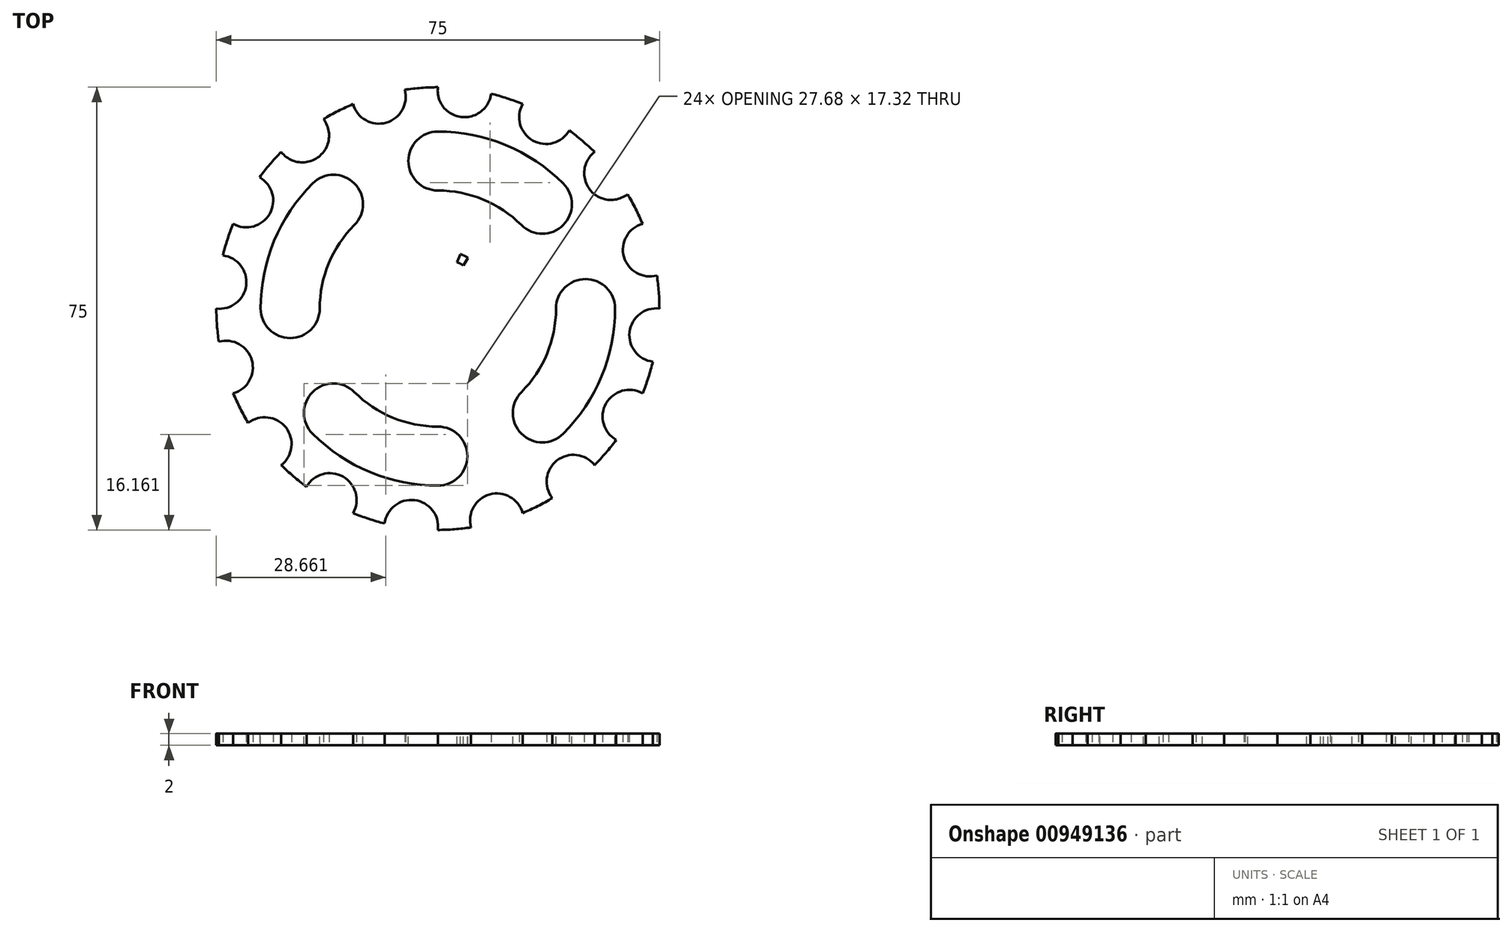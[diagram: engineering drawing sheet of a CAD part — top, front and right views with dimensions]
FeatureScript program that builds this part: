
annotation { "Feature Type Name" : "Feature", "Feature Type Description" : "" }
export const myFeature = defineFeature(function(context is Context, id is Id, definition is map)
    precondition{}
    {
        {
            var Q0;
            Q0=qCreatedBy(makeId("Top.planeOp"),FACE);
            var sketch = newSketch(context, id + "F0", { "sketchPlane" : qUnion([Q0])});
            skCircle(sketch, "E0", {"center": v(0, 0) * mm, "radius": 37.5 * mm});
            skArc(sketch, "E1", {"start": v(0, 37.5) * mm, "mid": v(3.95, 32.45) * mm, "end": v(9, 36.4) * mm});
            skArc(sketch, "E2.1.0", {"start": v(-14.35, 34.65) * mm, "mid": v(-8.77, 31.5) * mm, "end": v(-5.62, 37.08) * mm});
            skArc(sketch, "E2.2.0", {"start": v(-26.52, 26.52) * mm, "mid": v(-20.15, 25.74) * mm, "end": v(-19.38, 32.1) * mm});
            skArc(sketch, "E2.3.0", {"start": v(-34.65, 14.35) * mm, "mid": v(-28.47, 16.07) * mm, "end": v(-30.19, 22.25) * mm});
            skArc(sketch, "E2.4.0", {"start": v(-37.5, 0) * mm, "mid": v(-32.45, 3.95) * mm, "end": v(-36.4, 9) * mm});
            skArc(sketch, "E2.5.0", {"start": v(-34.65, -14.35) * mm, "mid": v(-31.5, -8.77) * mm, "end": v(-37.08, -5.62) * mm});
            skArc(sketch, "E2.6.0", {"start": v(-26.52, -26.52) * mm, "mid": v(-25.74, -20.15) * mm, "end": v(-32.1, -19.38) * mm});
            skArc(sketch, "E2.7.0", {"start": v(-14.35, -34.65) * mm, "mid": v(-16.07, -28.47) * mm, "end": v(-22.25, -30.19) * mm});
            skArc(sketch, "E2.8.0", {"start": v(0, -37.5) * mm, "mid": v(-3.95, -32.45) * mm, "end": v(-9, -36.4) * mm});
            skArc(sketch, "E2.9.0", {"start": v(14.35, -34.65) * mm, "mid": v(8.77, -31.5) * mm, "end": v(5.62, -37.08) * mm});
            skArc(sketch, "E2.10.0", {"start": v(26.52, -26.52) * mm, "mid": v(20.15, -25.74) * mm, "end": v(19.38, -32.1) * mm});
            skArc(sketch, "E2.11.0", {"start": v(34.65, -14.35) * mm, "mid": v(28.47, -16.07) * mm, "end": v(30.19, -22.25) * mm});
            skArc(sketch, "E2.12.0", {"start": v(37.5, 0) * mm, "mid": v(32.45, -3.95) * mm, "end": v(36.4, -9) * mm});
            skArc(sketch, "E2.13.0", {"start": v(34.65, 14.35) * mm, "mid": v(31.5, 8.77) * mm, "end": v(37.08, 5.62) * mm});
            skArc(sketch, "E2.14.0", {"start": v(26.52, 26.52) * mm, "mid": v(25.74, 20.15) * mm, "end": v(32.1, 19.38) * mm});
            skArc(sketch, "E2.15.0", {"start": v(14.35, 34.65) * mm, "mid": v(16.07, 28.47) * mm, "end": v(22.25, 30.19) * mm});
            skSolve(sketch);
        }
        {
            var Q0;
            {var subQ2=sQuery(id+"F0.wireOp",EDGE,"E1");Q0=makeQuery(id+"F0.imprint","IMPRINT",FACE,{"disambiguationData":[TD([[makeQuery(id+"F0.imprint","IMPRINT",EDGE,{"derivedFrom":subQ2}),-1.0]])]});}
            extrude(context, id + "F1", {"entities" : qUnion([Q0]), "depth" : 2 * mm, "offsetDistance" : 25 * mm});
        }
        {
            var Q0;
            Q0=makeQuery(id+"F1.opExtrude","CAP_FACE",FACE,{"disambiguationData":[OSD([sQuery(id+"F0.wireOp",EDGE,"E0"),sQuery(id+"F0.wireOp",EDGE,"E1"),sQuery(id+"F0.wireOp",EDGE,"E2.1.0"),sQuery(id+"F0.wireOp",EDGE,"E2.2.0"),sQuery(id+"F0.wireOp",EDGE,"E2.3.0"),sQuery(id+"F0.wireOp",EDGE,"E2.4.0"),sQuery(id+"F0.wireOp",EDGE,"E2.5.0"),sQuery(id+"F0.wireOp",EDGE,"E2.6.0"),sQuery(id+"F0.wireOp",EDGE,"E2.7.0"),sQuery(id+"F0.wireOp",EDGE,"E2.8.0"),sQuery(id+"F0.wireOp",EDGE,"E2.9.0"),sQuery(id+"F0.wireOp",EDGE,"E2.10.0"),sQuery(id+"F0.wireOp",EDGE,"E2.11.0"),sQuery(id+"F0.wireOp",EDGE,"E2.12.0"),sQuery(id+"F0.wireOp",EDGE,"E2.13.0"),sQuery(id+"F0.wireOp",EDGE,"E2.14.0"),sQuery(id+"F0.wireOp",EDGE,"E2.15.0")])],"isStart":false});
            var sketch = newSketch(context, id + "F2", { "sketchPlane" : qUnion([Q0])});
            skCircle(sketch, "E3", {"center": v(0, 0) * mm, "radius": 10 * mm});
            skArc(sketch, "E4", {"start": v(14.14, 14.14) * mm, "mid": v(7.65, 18.48) * mm, "end": v(0, 20) * mm});
            skArc(sketch, "E5", {"start": v(0, 30) * mm, "mid": v(-5, 25) * mm, "end": v(0, 20) * mm});
            skArc(sketch, "E6.1.0", {"start": v(-14.14, 14.14) * mm, "mid": v(-14.14, 21.21) * mm, "end": v(-21.21, 21.21) * mm});
            skArc(sketch, "E6.2.0", {"start": v(-30, 0) * mm, "mid": v(-25, -5) * mm, "end": v(-20, 0) * mm});
            skArc(sketch, "E6.3.0", {"start": v(-14.14, -14.14) * mm, "mid": v(-21.21, -14.14) * mm, "end": v(-21.21, -21.21) * mm});
            skArc(sketch, "E6.4.0", {"start": v(0, -30) * mm, "mid": v(5, -25) * mm, "end": v(0, -20) * mm});
            skArc(sketch, "E6.5.0", {"start": v(14.14, -14.14) * mm, "mid": v(14.14, -21.21) * mm, "end": v(21.21, -21.21) * mm});
            skArc(sketch, "E6.6.0", {"start": v(30, 0) * mm, "mid": v(25, 5) * mm, "end": v(20, 0) * mm});
            skArc(sketch, "E6.7.0", {"start": v(14.14, 14.14) * mm, "mid": v(21.21, 14.14) * mm, "end": v(21.21, 21.21) * mm});
            skArc(sketch, "E7.trimOffspring", {"start": v(14.14, -14.14) * mm, "mid": v(18.48, -7.65) * mm, "end": v(20, 0) * mm});
            skArc(sketch, "E8.trimOffspring", {"start": v(-14.14, -14.14) * mm, "mid": v(-7.65, -18.48) * mm, "end": v(0, -20) * mm});
            skArc(sketch, "E9.trimOffspring", {"start": v(-14.14, 14.14) * mm, "mid": v(-18.48, 7.65) * mm, "end": v(-20, 0) * mm});
            skArc(sketch, "E10.trimOffspring", {"start": v(-21.21, -21.21) * mm, "mid": v(-11.48, -27.72) * mm, "end": v(0, -30) * mm});
            skArc(sketch, "E11.trimOffspring", {"start": v(21.21, -21.21) * mm, "mid": v(27.72, -11.48) * mm, "end": v(30, 0) * mm});
            skArc(sketch, "E12.trimOffspring", {"start": v(21.21, 21.21) * mm, "mid": v(11.48, 27.72) * mm, "end": v(0, 30) * mm});
            skArc(sketch, "E13", {"start": v(-21.21, 21.21) * mm, "mid": v(-27.72, 11.48) * mm, "end": v(-30, 0) * mm});
            skSolve(sketch);
        }
        {
            var Q0;
            Q0=makeQuery(id+"F2.imprint","IMPRINT",FACE,{"disambiguationData":[TD([[makeQuery(id+"F2.imprint","IMPRINT",EDGE,{"derivedFrom":sQuery(id+"F2.wireOp",EDGE,"E6.1.0")}),1.0]])]});
            var Q1;
            Q1=makeQuery(id+"F2.imprint","IMPRINT",FACE,{"disambiguationData":[TD([[makeQuery(id+"F2.imprint","IMPRINT",EDGE,{"derivedFrom":sQuery(id+"F2.wireOp",EDGE,"E4")}),-1.0]])]});
            var Q2;
            Q2=makeQuery(id+"F2.imprint","IMPRINT",FACE,{"disambiguationData":[TD([[makeQuery(id+"F2.imprint","IMPRINT",EDGE,{"derivedFrom":sQuery(id+"F2.wireOp",EDGE,"E6.5.0")}),1.0]])]});
            var Q3;
            Q3=makeQuery(id+"F2.imprint","IMPRINT",FACE,{"disambiguationData":[TD([[makeQuery(id+"F2.imprint","IMPRINT",EDGE,{"derivedFrom":sQuery(id+"F2.wireOp",EDGE,"E6.3.0")}),1.0]])]});
            extrude(context, id + "F3", {"entities" : qUnion([Q0, Q1, Q2, Q3]), "operationType" : NewBodyOperationType.REMOVE, "oppositeDirection" : true, "depth" : 25 * mm, "offsetDistance" : 25 * mm});
        }
        {
            var Q0;
            Q0=makeQuery(id+"F1.opExtrude","CAP_FACE",FACE,{"disambiguationData":[OSD([sQuery(id+"F0.wireOp",EDGE,"E0"),sQuery(id+"F0.wireOp",EDGE,"E1"),sQuery(id+"F0.wireOp",EDGE,"E2.1.0"),sQuery(id+"F0.wireOp",EDGE,"E2.2.0"),sQuery(id+"F0.wireOp",EDGE,"E2.3.0"),sQuery(id+"F0.wireOp",EDGE,"E2.4.0"),sQuery(id+"F0.wireOp",EDGE,"E2.5.0"),sQuery(id+"F0.wireOp",EDGE,"E2.6.0"),sQuery(id+"F0.wireOp",EDGE,"E2.7.0"),sQuery(id+"F0.wireOp",EDGE,"E2.8.0"),sQuery(id+"F0.wireOp",EDGE,"E2.9.0"),sQuery(id+"F0.wireOp",EDGE,"E2.10.0"),sQuery(id+"F0.wireOp",EDGE,"E2.11.0"),sQuery(id+"F0.wireOp",EDGE,"E2.12.0"),sQuery(id+"F0.wireOp",EDGE,"E2.13.0"),sQuery(id+"F0.wireOp",EDGE,"E2.14.0"),sQuery(id+"F0.wireOp",EDGE,"E2.15.0")])],"isStart":false});
            var sketch = newSketch(context, id + "F4", { "sketchPlane" : qUnion([Q0])});
            skCircle(sketch, "E14", {"center": v(0, 0) * mm, "radius": 10 * mm});
            skArc(sketch, "E15", {"start": v(3.25, 7.85) * mm, "mid": v(3.8, 7.6) * mm, "end": v(4.35, 7.3) * mm});
            skLineSegment(sketch, "E16", {"start": v(4.35, 7.3) * mm, "end": v(5.11, 8.6) * mm});
            skLineSegment(sketch, "E17", {"start": v(3.25, 7.85) * mm, "end": v(3.83, 9.24) * mm});
            skLineSegment(sketch, "E18.1.0", {"start": v(-1.1, 8.43) * mm, "end": v(-1.3, 9.91) * mm});
            skLineSegment(sketch, "E18.1.1", {"start": v(0.11, 8.5) * mm, "end": v(0.13, 10) * mm});
            skArc(sketch, "E18.1.2", {"start": v(-1.1, 8.43) * mm, "mid": v(-0.5, 8.49) * mm, "end": v(0.11, 8.5) * mm});
            skLineSegment(sketch, "E18.2.0", {"start": v(-5.17, 6.74) * mm, "end": v(-6.09, 7.93) * mm});
            skLineSegment(sketch, "E18.2.1", {"start": v(-4.15, 7.42) * mm, "end": v(-4.89, 8.73) * mm});
            skArc(sketch, "E18.2.2", {"start": v(-5.17, 6.74) * mm, "mid": v(-4.68, 7.1) * mm, "end": v(-4.15, 7.42) * mm});
            skLineSegment(sketch, "E18.3.0", {"start": v(-7.85, 3.25) * mm, "end": v(-9.24, 3.83) * mm});
            skLineSegment(sketch, "E18.3.1", {"start": v(-7.3, 4.35) * mm, "end": v(-8.6, 5.11) * mm});
            skArc(sketch, "E18.3.2", {"start": v(-7.85, 3.25) * mm, "mid": v(-7.6, 3.8) * mm, "end": v(-7.3, 4.35) * mm});
            skLineSegment(sketch, "E18.4.0", {"start": v(-8.43, -1.1) * mm, "end": v(-9.91, -1.3) * mm});
            skLineSegment(sketch, "E18.4.1", {"start": v(-8.5, 0.11) * mm, "end": v(-10, 0.13) * mm});
            skArc(sketch, "E18.4.2", {"start": v(-8.43, -1.1) * mm, "mid": v(-8.49, -0.5) * mm, "end": v(-8.5, 0.11) * mm});
            skLineSegment(sketch, "E18.5.0", {"start": v(-6.74, -5.17) * mm, "end": v(-7.93, -6.09) * mm});
            skLineSegment(sketch, "E18.5.1", {"start": v(-7.42, -4.15) * mm, "end": v(-8.73, -4.89) * mm});
            skArc(sketch, "E18.5.2", {"start": v(-6.74, -5.17) * mm, "mid": v(-7.1, -4.68) * mm, "end": v(-7.42, -4.15) * mm});
            skLineSegment(sketch, "E18.6.0", {"start": v(-3.25, -7.85) * mm, "end": v(-3.83, -9.24) * mm});
            skLineSegment(sketch, "E18.6.1", {"start": v(-4.35, -7.3) * mm, "end": v(-5.11, -8.6) * mm});
            skArc(sketch, "E18.6.2", {"start": v(-3.25, -7.85) * mm, "mid": v(-3.8, -7.6) * mm, "end": v(-4.35, -7.3) * mm});
            skLineSegment(sketch, "E18.7.0", {"start": v(1.1, -8.43) * mm, "end": v(1.3, -9.91) * mm});
            skLineSegment(sketch, "E18.7.1", {"start": v(-0.11, -8.5) * mm, "end": v(-0.13, -10) * mm});
            skArc(sketch, "E18.7.2", {"start": v(1.1, -8.43) * mm, "mid": v(0.5, -8.49) * mm, "end": v(-0.11, -8.5) * mm});
            skLineSegment(sketch, "E18.8.0", {"start": v(5.17, -6.74) * mm, "end": v(6.09, -7.93) * mm});
            skLineSegment(sketch, "E18.8.1", {"start": v(4.15, -7.42) * mm, "end": v(4.89, -8.73) * mm});
            skArc(sketch, "E18.8.2", {"start": v(5.17, -6.74) * mm, "mid": v(4.68, -7.1) * mm, "end": v(4.15, -7.42) * mm});
            skLineSegment(sketch, "E18.9.0", {"start": v(7.85, -3.25) * mm, "end": v(9.24, -3.83) * mm});
            skLineSegment(sketch, "E18.9.1", {"start": v(7.3, -4.35) * mm, "end": v(8.6, -5.11) * mm});
            skArc(sketch, "E18.9.2", {"start": v(7.85, -3.25) * mm, "mid": v(7.6, -3.8) * mm, "end": v(7.3, -4.35) * mm});
            skLineSegment(sketch, "E18.10.0", {"start": v(8.43, 1.1) * mm, "end": v(9.91, 1.3) * mm});
            skLineSegment(sketch, "E18.10.1", {"start": v(8.5, -0.11) * mm, "end": v(10, -0.13) * mm});
            skArc(sketch, "E18.10.2", {"start": v(8.43, 1.1) * mm, "mid": v(8.49, 0.5) * mm, "end": v(8.5, -0.11) * mm});
            skLineSegment(sketch, "E18.11.0", {"start": v(6.74, 5.17) * mm, "end": v(7.93, 6.09) * mm});
            skLineSegment(sketch, "E18.11.1", {"start": v(7.42, 4.15) * mm, "end": v(8.73, 4.89) * mm});
            skArc(sketch, "E18.11.2", {"start": v(6.74, 5.17) * mm, "mid": v(7.1, 4.68) * mm, "end": v(7.42, 4.15) * mm});
            skSolve(sketch);
        }
        {
            var Q0;
            Q0=makeQuery(id+"F4.imprint","IMPRINT",FACE,{"disambiguationData":[TD([[makeQuery(id+"F4.imprint","IMPRINT",EDGE,{"derivedFrom":sQuery(id+"F4.wireOp",EDGE,"E15")}),-1.0]])]});
            extrude(context, id + "F5", {"entities" : qUnion([Q0]), "operationType" : NewBodyOperationType.REMOVE, "oppositeDirection" : true, "depth" : 2 * mm, "offsetDistance" : 25 * mm});
        }
    });
